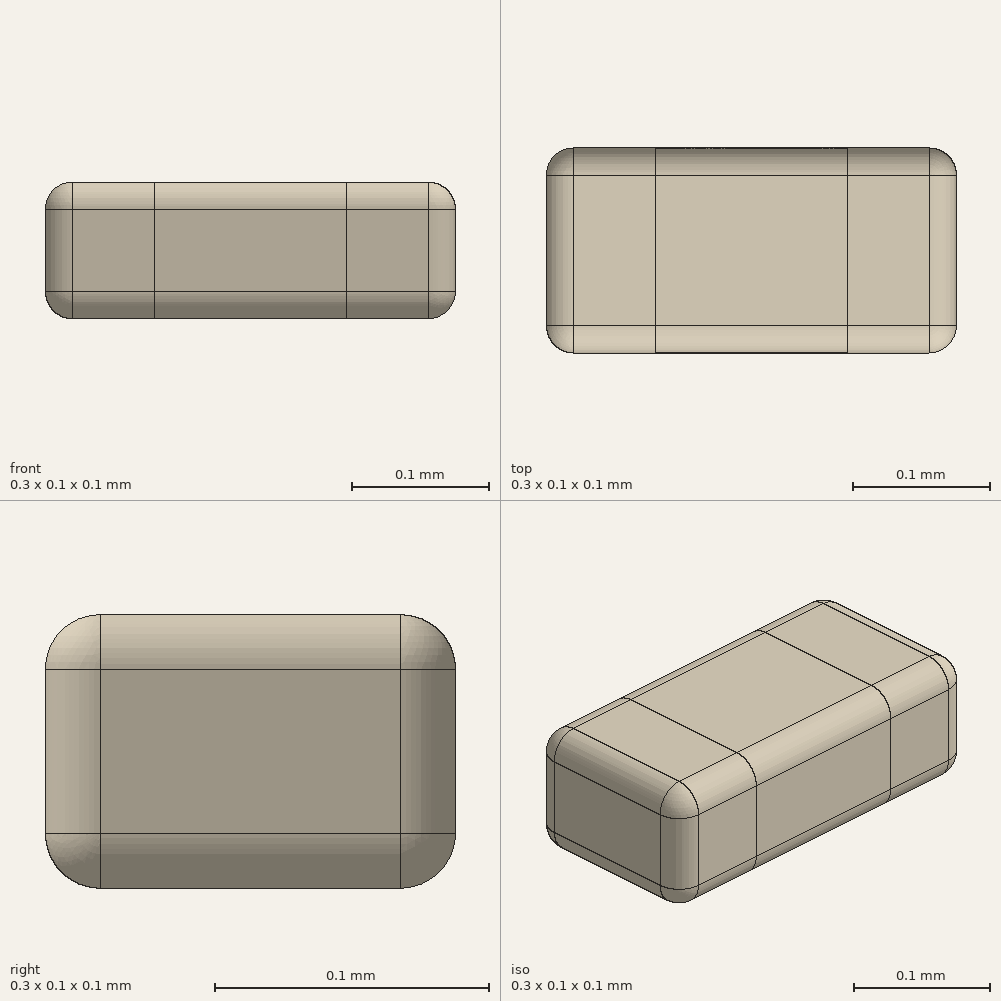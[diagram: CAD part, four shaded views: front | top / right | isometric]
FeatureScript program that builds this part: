
annotation { "Feature Type Name" : "Feature", "Feature Type Description" : "" }
export const myFeature = defineFeature(function(context is Context, id is Id, definition is map)
    precondition{}
    {
        {
            assignVariable(context, id + "F0", {"name" : "H", "anyValue" : 0.1});
        }
        {
            assignVariable(context, id + "F1", {"name" : "r", "anyValue" : 0.02});
        }
        {
            var Q0;
            Q0=qCreatedBy(makeId("Top.planeOp"),FACE);
            var sketch = newSketch(context, id + "F2", { "sketchPlane" : qUnion([Q0])});
            skLineSegment(sketch, "E0.bottom", {"start": v(0.07, 0.07) * mm, "end": v(-0.07, 0.07) * mm});
            skLineSegment(sketch, "E0.top", {"start": v(0.07, -0.08) * mm, "end": v(-0.07, -0.08) * mm});
            skLineSegment(sketch, "E0.left", {"start": v(0.07, 0.07) * mm, "end": v(0.07, -0.07) * mm});
            skLineSegment(sketch, "E0.right", {"start": v(-0.07, 0.07) * mm, "end": v(-0.07, -0.07) * mm});
            skPoint(sketch, "E0.middle", {"position": v(0, 0) * mm});
            skLineSegment(sketch, "E1", {"start": v(0.07, 0.08) * mm, "end": v(0.15, 0.08) * mm});
            skLineSegment(sketch, "E2", {"start": v(0.15, 0.08) * mm, "end": v(0.15, -0.07) * mm});
            skLineSegment(sketch, "E3", {"start": v(0.15, -0.07) * mm, "end": v(0.07, -0.07) * mm});
            skLineSegment(sketch, "E4", {"start": v(-0.07, 0.07) * mm, "end": v(-0.15, 0.07) * mm});
            skLineSegment(sketch, "E5", {"start": v(-0.15, 0.07) * mm, "end": v(-0.15, -0.07) * mm});
            skLineSegment(sketch, "E6", {"start": v(-0.15, -0.07) * mm, "end": v(-0.07, -0.07) * mm});
            skSolve(sketch);
        }
        {
            var Q0;
            Q0=makeQuery(id+"F2.imprint","IMPRINT",FACE,{"disambiguationData":[TD([[makeQuery(id+"F2.imprint","IMPRINT",EDGE,{"derivedFrom":sQuery(id+"F2.wireOp",EDGE,"E0.bottom")}),1.0]])]});
            extrude(context, id + "F3", {"entities" : qUnion([Q0]), "depth" : (getVariable(context, 'H')) * mm - (getVariable(context, 'r')) * mm});
        }
        {
            var Q0;
            Q0=makeQuery(id+"F2.imprint","IMPRINT",FACE,{"disambiguationData":[TD([[makeQuery(id+"F2.imprint","IMPRINT",EDGE,{"derivedFrom":sQuery(id+"F2.wireOp",EDGE,"E0.right")}),-1.0]])]});
            extrude(context, id + "F4", {"entities" : qUnion([Q0]), "depth" : (getVariable(context, 'H')) * mm});
        }
        {
            var Q0;
            Q0=makeQuery(id+"F2.imprint","IMPRINT",FACE,{"disambiguationData":[TD([[makeQuery(id+"F2.imprint","IMPRINT",EDGE,{"derivedFrom":sQuery(id+"F2.wireOp",EDGE,"E0.left")}),1.0]])]});
            extrude(context, id + "F5", {"entities" : qUnion([Q0]), "depth" : (getVariable(context, 'H')) * mm});
        }
        {
            var Q0;
            Q0=makeQuery(id+"F3.opExtrude","CAP_FACE",FACE,{"disambiguationData":[OSD([sQuery(id+"F2.wireOp",EDGE,"E0.bottom"),sQuery(id+"F2.wireOp",EDGE,"E0.top"),sQuery(id+"F2.wireOp",EDGE,"E0.left"),sQuery(id+"F2.wireOp",EDGE,"E0.right")])],"isStart":false});
            extrude(context, id + "F6", {"entities" : qUnion([Q0]), "depth" : (getVariable(context, 'r')) * mm});
        }
        {
            var Q0;
            Q0=makeQuery(id+"F4.opExtrude","CAP_EDGE",EDGE,{"disambiguationData":[OSD([sQuery(id+"F2.wireOp",EDGE,"E6")])],"isStart":false});
            var Q1;
            Q1=makeQuery(id+"F5.opExtrude","CAP_EDGE",EDGE,{"disambiguationData":[OSD([sQuery(id+"F2.wireOp",EDGE,"E3")])],"isStart":false});
            var Q2;
            Q2=makeQuery(id+"F5.opExtrude","SWEPT_EDGE",EDGE,{"disambiguationData":[OSD([sQuery(id+"F2.wireOp",EDGE,"E2"),sQuery(id+"F2.wireOp",EDGE,"E3")])]});
            var Q3;
            Q3=makeQuery(id+"F5.opExtrude","SWEPT_FACE",FACE,{"disambiguationData":[OSD([sQuery(id+"F2.wireOp",EDGE,"E2")])]});
            var Q4;
            Q4=makeQuery(id+"F4.opExtrude","SWEPT_FACE",FACE,{"disambiguationData":[OSD([sQuery(id+"F2.wireOp",EDGE,"E5")])]});
            var Q5;
            Q5=makeQuery(id+"F4.opExtrude","CAP_EDGE",EDGE,{"disambiguationData":[OSD([sQuery(id+"F2.wireOp",EDGE,"E4")])],"isStart":false});
            var Q6;
            Q6=makeQuery(id+"F3.opExtrude","CAP_EDGE",EDGE,{"disambiguationData":[OSD([sQuery(id+"F2.wireOp",EDGE,"E0.bottom")])],"isStart":true});
            var Q7;
            Q7=makeQuery(id+"F4.opExtrude","CAP_EDGE",EDGE,{"disambiguationData":[OSD([sQuery(id+"F2.wireOp",EDGE,"E4")])],"isStart":true});
            var Q8;
            Q8=makeQuery(id+"F5.opExtrude","CAP_EDGE",EDGE,{"disambiguationData":[OSD([sQuery(id+"F2.wireOp",EDGE,"E1")])],"isStart":false});
            var Q9;
            Q9=makeQuery(id+"F5.opExtrude","CAP_EDGE",EDGE,{"disambiguationData":[OSD([sQuery(id+"F2.wireOp",EDGE,"E1")])],"isStart":true});
            var Q10;
            Q10=makeQuery(id+"F6.opExtrude","CAP_EDGE",EDGE,{"disambiguationData":[OSD([sQuery(id+"F2.wireOp",EDGE,"E0.top")])],"isStart":false});
            var Q11;
            Q11=makeQuery(id+"F6.opExtrude","CAP_EDGE",EDGE,{"disambiguationData":[OSD([sQuery(id+"F2.wireOp",EDGE,"E0.bottom")])],"isStart":false});
            var Q12;
            Q12=makeQuery(id+"F4.opExtrude","CAP_EDGE",EDGE,{"disambiguationData":[OSD([sQuery(id+"F2.wireOp",EDGE,"E6")])],"isStart":true});
            var Q13;
            Q13=makeQuery(id+"F3.opExtrude","CAP_EDGE",EDGE,{"disambiguationData":[OSD([sQuery(id+"F2.wireOp",EDGE,"E0.top")])],"isStart":true});
            var Q14;
            Q14=makeQuery(id+"F5.opExtrude","CAP_EDGE",EDGE,{"disambiguationData":[OSD([sQuery(id+"F2.wireOp",EDGE,"E3")])],"isStart":true});
            fillet(context, id + "F7", {"entities" : qUnion([Q0, Q1, Q2, Q3, Q4, Q5, Q6, Q7, Q8, Q9, Q10, Q11, Q12, Q13, Q14]), "radius" : (getVariable(context, 'r')) * mm, "tangentPropagation" : true, "allowEdgeOverflow" : false});
        }
    });
